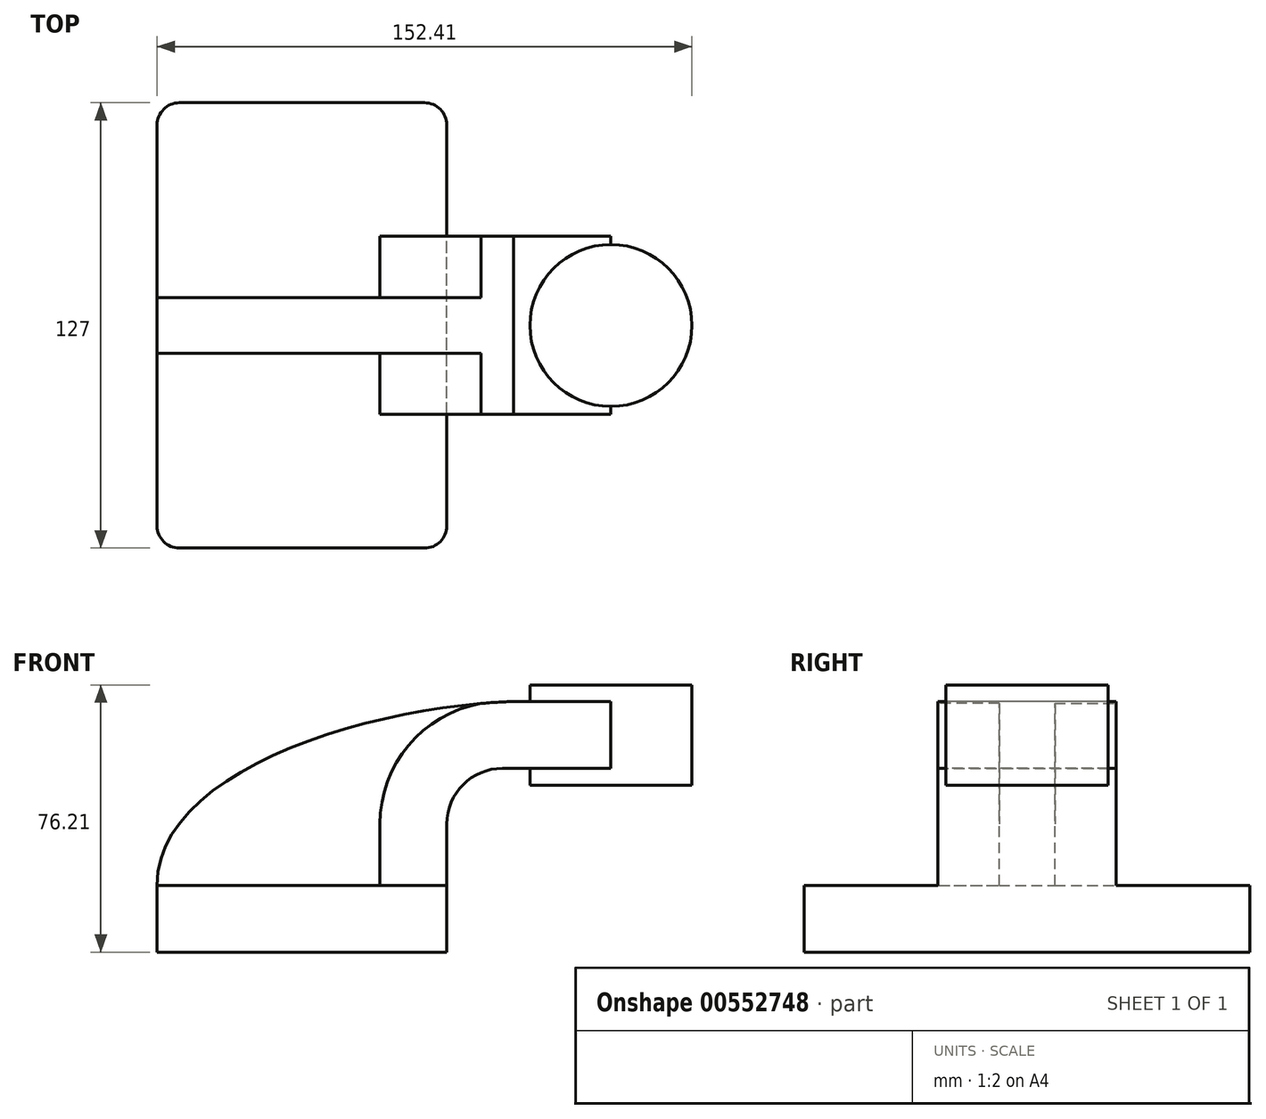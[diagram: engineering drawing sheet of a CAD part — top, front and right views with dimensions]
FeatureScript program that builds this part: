
annotation { "Feature Type Name" : "Feature", "Feature Type Description" : "" }
export const myFeature = defineFeature(function(context is Context, id is Id, definition is map)
    precondition{}
    {
        {
            var Q0;
            Q0=qCreatedBy(makeId("Front.planeOp"),FACE);
            var sketch = newSketch(context, id + "F0", { "sketchPlane" : qUnion([Q0])});
            skLineSegment(sketch, "E0.bottom", {"start": v(41.27, 9.53) * mm, "end": v(-41.28, 9.53) * mm});
            skLineSegment(sketch, "E0.top", {"start": v(41.28, -9.52) * mm, "end": v(-41.27, -9.52) * mm});
            skLineSegment(sketch, "E0.left", {"start": v(41.28, 9.53) * mm, "end": v(41.28, -9.52) * mm});
            skLineSegment(sketch, "E0.right", {"start": v(-41.28, 9.53) * mm, "end": v(-41.27, -9.52) * mm});
            skPoint(sketch, "E0.middle", {"position": v(0, 0) * mm});
            skLineSegment(sketch, "E1.bottom", {"start": v(60.33, 38.1) * mm, "end": v(111.12, 38.1) * mm});
            skLineSegment(sketch, "E1.top", {"start": v(60.33, 66.68) * mm, "end": v(111.12, 66.68) * mm});
            skLineSegment(sketch, "E1.left", {"start": v(60.33, 38.1) * mm, "end": v(60.32, 66.68) * mm});
            skLineSegment(sketch, "E1.right", {"start": v(111.12, 38.1) * mm, "end": v(111.12, 66.68) * mm});
            skPoint(sketch, "E1.middle", {"position": v(85.72, 52.39) * mm});
            skLineSegment(sketch, "E2", {"start": v(41.27, 9.53) * mm, "end": v(41.27, 27) * mm});
            skArc(sketch, "E3", {"start": v(41.27, 27) * mm, "mid": v(45.92, 38.23) * mm, "end": v(57.15, 42.88) * mm});
            skLineSegment(sketch, "E4", {"start": v(57.15, 42.88) * mm, "end": v(88.03, 42.88) * mm});
            skLineSegment(sketch, "E5.0", {"start": v(57.15, 61.93) * mm, "end": v(88.03, 61.93) * mm});
            skArc(sketch, "E5.1", {"start": v(22.23, 27) * mm, "mid": v(32.45, 51.7) * mm, "end": v(57.15, 61.93) * mm});
            skLineSegment(sketch, "E5.2", {"start": v(22.22, 9.53) * mm, "end": v(22.22, 27) * mm});
            skLineSegment(sketch, "E6", {"start": v(88.03, 66.68) * mm, "end": v(88.03, 38.1) * mm});
            skFitSpline(sketch, "E7", {"points": [v(-41.28, 9.53) * mm, v(60.33, 61.93) * mm], "startDerivative": vector(-1.07, 97.1) * mm, "endDerivative": vector(125.51, 3.8) * mm});
            skSolve(sketch);
        }
        {
            var Q0;
            Q0=makeQuery(id+"F0.imprint","IMPRINT",FACE,{"disambiguationData":[TD([[makeQuery(id+"F0.imprint","IMPRINT",EDGE,{"derivedFrom":sQuery(id+"F0.wireOp",EDGE,"E0.top")}),-1.0]])]});
            extrude(context, id + "F1", {"entities" : qUnion([Q0]), "endBound" : BoundingType.SYMMETRIC, "depth" : 127 * mm, "offsetDistance" : 25.4 * mm});
        }
        {
            var Q0;
            {var subQ1=sQuery(id+"F0.wireOp",EDGE,"E2");Q0=makeQuery(id+"F0.imprint","IMPRINT",FACE,{"disambiguationData":[TD([[makeQuery(id+"F0.imprint","IMPRINT",EDGE,{"derivedFrom":subQ1}),1.0]])]});}
            extrude(context, id + "F2", {"entities" : qUnion([Q0]), "operationType" : NewBodyOperationType.ADD, "endBound" : BoundingType.SYMMETRIC, "depth" : 50.8 * mm, "offsetDistance" : 25.4 * mm});
        }
        {
            var Q0;
            {var subQ3=sQuery(id+"F0.wireOp",EDGE,"E5.2");Q0=makeQuery(id+"F0.imprint","IMPRINT",FACE,{"disambiguationData":[TD([[makeQuery(id+"F0.imprint","IMPRINT",EDGE,{"derivedFrom":subQ3}),1.0]])]});}
            extrude(context, id + "F3", {"entities" : qUnion([Q0]), "operationType" : NewBodyOperationType.ADD, "endBound" : BoundingType.SYMMETRIC, "depth" : 15.88 * mm, "offsetDistance" : 25.4 * mm});
        }
        {
            var Q0;
            {var subQ3=sQuery(id+"F0.wireOp",EDGE,"E4");var subQ5=sQuery(id+"F0.wireOp",EDGE,"E6");var subQ6=makeQuery(id+"F0.imprint","INTERSECT",VERTEX,{"derivedFrom":[subQ3,subQ5]});Q0=makeQuery(id+"F0.imprint","IMPRINT",FACE,{"disambiguationData":[TD([[makeQuery(id+"F0.imprint","IMPRINT",EDGE,{"disambiguationData":[TD([[subQ6,1.0]])],"derivedFrom":subQ3}),1.0]])]});}
            extrude(context, id + "F4", {"entities" : qUnion([Q0]), "operationType" : NewBodyOperationType.ADD, "endBound" : BoundingType.SYMMETRIC, "depth" : 50.8 * mm, "offsetDistance" : 25.4 * mm});
        }
        {
            var Q0;
            {var subQ4=sQuery(id+"F0.wireOp",EDGE,"E1.right");Q0=makeQuery(id+"F0.imprint","IMPRINT",FACE,{"disambiguationData":[TD([[makeQuery(id+"F0.imprint","IMPRINT",EDGE,{"derivedFrom":subQ4}),1.0]])]});}
            var Q1;
            Q1=sQuery(id+"F0.wireOp",EDGE,"E6");
            revolve(context, id + "F5", {"operationType" : NewBodyOperationType.ADD, "surfaceOperationType" : NewSurfaceOperationType.NEW, "entities" : qUnion([Q0]), "axis" : qUnion([Q1]), "revolveType" : RevolveType.FULL});
        }
        {
            var Q0;
            Q0=makeQuery(id+"F1.opExtrude","CAP_EDGE",EDGE,{"disambiguationData":[OSD([sQuery(id+"F0.wireOp",EDGE,"E0.left")])],"isStart":false});
            var Q1;
            Q1=makeQuery(id+"F1.opExtrude","CAP_EDGE",EDGE,{"disambiguationData":[OSD([sQuery(id+"F0.wireOp",EDGE,"E0.right")])],"isStart":false});
            var Q2;
            Q2=makeQuery(id+"F1.opExtrude","CAP_EDGE",EDGE,{"disambiguationData":[OSD([sQuery(id+"F0.wireOp",EDGE,"E0.right")])],"isStart":true});
            var Q3;
            Q3=makeQuery(id+"F1.opExtrude","CAP_EDGE",EDGE,{"disambiguationData":[OSD([sQuery(id+"F0.wireOp",EDGE,"E0.left")])],"isStart":true});
            fillet(context, id + "F6", {"entities" : qUnion([Q0, Q1, Q2, Q3]), "radius" : 6.35 * mm, "tangentPropagation" : true, "allowEdgeOverflow" : false});
        }
    });
